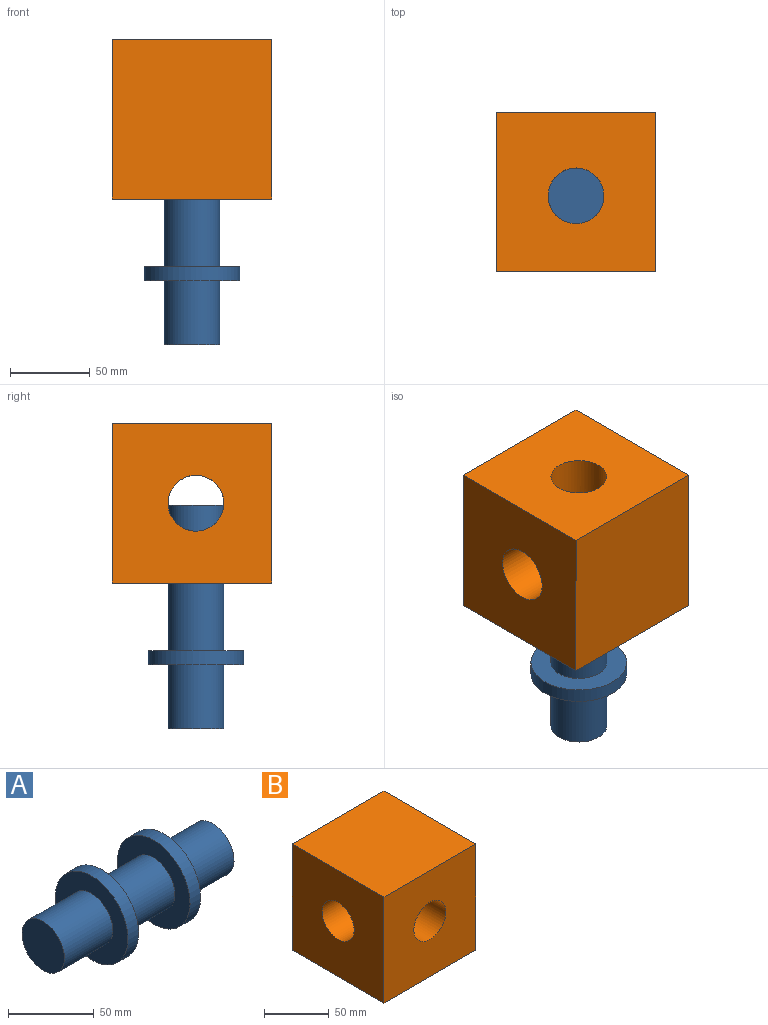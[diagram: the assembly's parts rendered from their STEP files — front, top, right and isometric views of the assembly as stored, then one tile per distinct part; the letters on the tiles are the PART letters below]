
ASSEMBLY  parts=2 mates=1
PART A: 11 faces, bbox 140x60x60 mm
  f0: plane 35x35mm, normal (1,0,0), area 962.1mm2, adj f1
  f1: cylinder r=17.5mm len=40mm, axis (-1,0,0), area 4398.2mm2, adj f0,f2
  f2: plane 60x60mm, normal (1,0,0), area 1865.3mm2, adj f1,f3
  f3: cylinder r=30mm len=60mm, axis (-1,0,0), area 1655.5mm2, adj f2,f4
  f4: plane 60x60mm, normal (-1,0,0), area 1865.3mm2, adj f3,f5
  f5: cylinder r=17.5mm len=42.43mm, axis (-1,0,0), area 4665.9mm2, adj f4,f10
  f6: plane 35x35mm, normal (-1,0,0), area 962.1mm2, adj f7
  f7: cylinder r=17.5mm len=40mm, axis (1,0,0), area 4398.2mm2, adj f6,f8
  f8: plane 60x60mm, normal (-1,0,0), area 1865.3mm2, adj f7,f9
  f9: cylinder r=30mm len=60mm, axis (1,0,0), area 1655.5mm2, adj f8,f10
  f10: plane 60x60mm, normal (1,0,0), area 1865.3mm2, adj f5,f9
PART B: 9 faces, bbox 100x100x100 mm
  f0: plane 100x100mm, normal (0,0,1), area 10000mm2, adj f1,f3,f4,f5
  f1: plane 100x100mm, normal (-1,0,0), area 9040.3mm2, adj f0,f2,f4,f5,f8
  f2: plane 100x100mm, normal (0,0,-1), area 10000mm2, adj f1,f3,f4,f5
  f3: plane 100x100mm, normal (1,0,0), area 9040.3mm2, adj f0,f2,f4,f5,f7
  f4: plane 100x100mm, normal (0,-1,0), area 9037.9mm2, adj f0,f1,f2,f3,f6
  f5: plane 100x100mm, normal (0,1,0), area 9037.9mm2, adj f0,f1,f2,f3,f6
  f6: cylinder r=17.5mm len=100mm, axis (0,1,0), area 8559.8mm2, adj f4,f5,f7,f8
  f7: cylinder r=17.48mm len=49.14mm, axis (1,0,0), area 4306.8mm2, adj f3,f6
  f8: cylinder r=17.48mm len=49.14mm, axis (1,0,0), area 4214.6mm2, adj f1,f6
PLACE A rot(axis=(-0.71,0,-0.71),180deg) t=(51.77,33.56,-157.45)mm
PLACE B rot(axis=(0.58,0.58,-0.58),120deg) t=(51.77,33.56,-86.23)mm
MATE fastened A.f1 <-> B.f7  axis (0,0,-1) through (51.77,33.56,-136.23)mm
